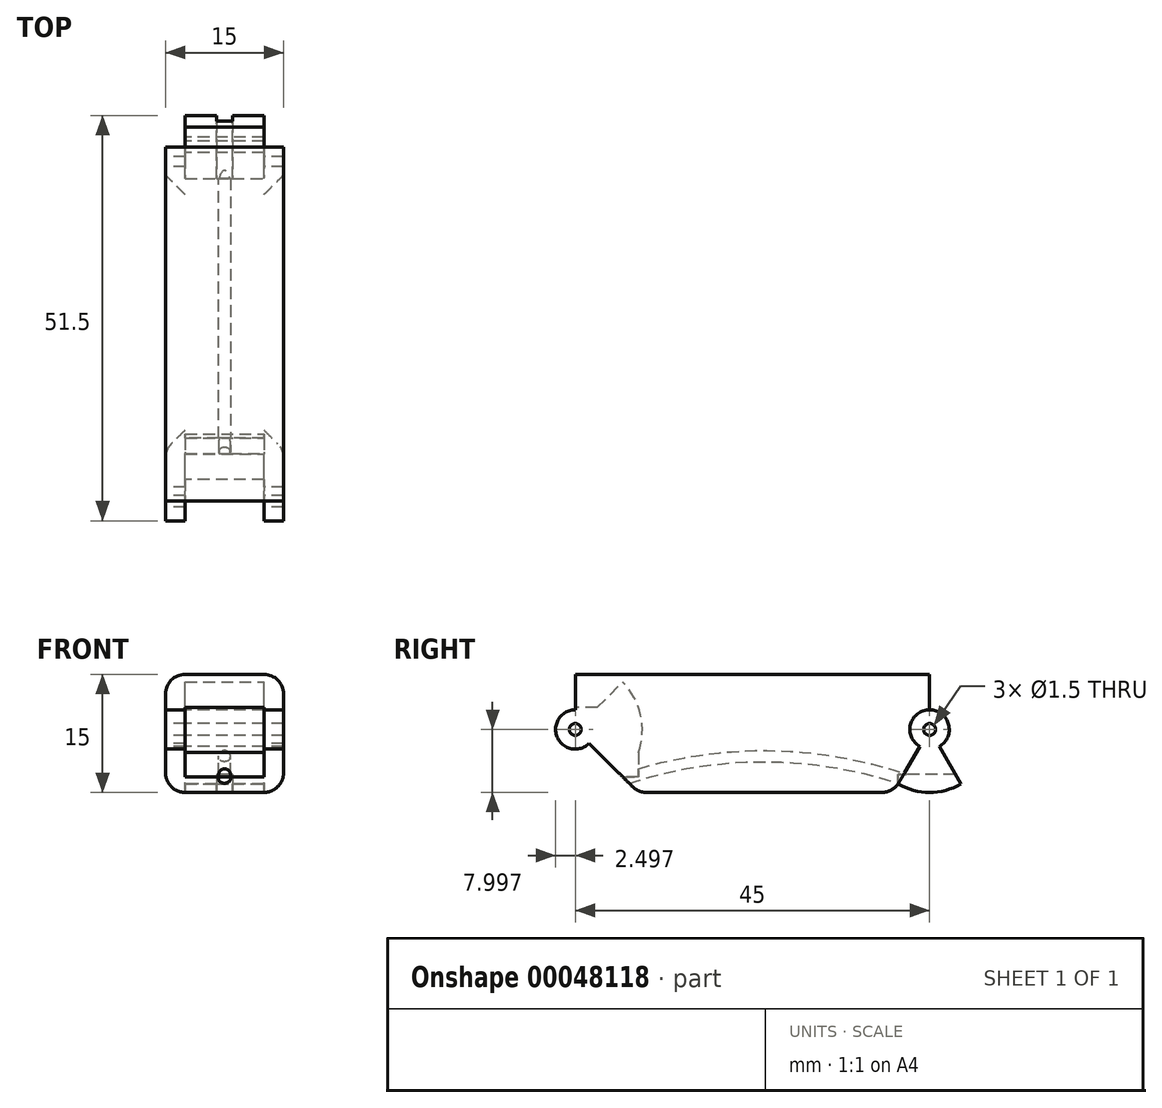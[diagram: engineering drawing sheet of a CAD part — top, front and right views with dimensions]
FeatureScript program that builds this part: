
annotation { "Feature Type Name" : "Feature", "Feature Type Description" : "" }
export const myFeature = defineFeature(function(context is Context, id is Id, definition is map)
    precondition{}
    {
        {
            var Q0;
            Q0=qCreatedBy(makeId("Right.planeOp"),FACE);
            var sketch = newSketch(context, id + "F0", { "sketchPlane" : qUnion([Q0])});
            skLineSegment(sketch, "E0.bottom", {"start": v(-42.54, 1.89) * mm, "end": v(2.46, 1.89) * mm});
            skLineSegment(sketch, "E0.top", {"start": v(-42.54, -13.11) * mm, "end": v(2.46, -13.11) * mm});
            skLineSegment(sketch, "E0.left", {"start": v(-42.54, 1.89) * mm, "end": v(-42.54, -13.11) * mm});
            skLineSegment(sketch, "E0.right", {"start": v(2.46, 1.89) * mm, "end": v(2.46, -13.11) * mm});
            skCircle(sketch, "E1", {"center": v(2.46, -5.11) * mm, "radius": 2.5 * mm});
            skCircle(sketch, "E2", {"center": v(2.46, -5.11) * mm, "radius": 8 * mm});
            skLineSegment(sketch, "E3", {"start": v(2.46, -5.11) * mm, "end": v(6.46, -12.04) * mm});
            skCircle(sketch, "E4", {"center": v(2.46, -5.11) * mm, "radius": 0.75 * mm});
            skLineSegment(sketch, "E5", {"start": v(2.46, -5.11) * mm, "end": v(-2.16, -13.11) * mm});
            skCircle(sketch, "E6", {"center": v(-42.54, -5.11) * mm, "radius": 2.5 * mm});
            skCircle(sketch, "E7", {"center": v(-42.54, -5.11) * mm, "radius": 0.75 * mm});
            skLineSegment(sketch, "E8", {"start": v(-42.54, -5.11) * mm, "end": v(-34.54, -13.11) * mm});
            skArc(sketch, "E9", {"start": v(-36.52, -11.13) * mm, "mid": v(-34.03, -5.11) * mm, "end": v(-36.52, 0.9) * mm});
            skLineSegment(sketch, "E10", {"start": v(-42.54, -5.11) * mm, "end": v(-35.54, 1.89) * mm});
            skSolve(sketch);
        }
        {
            var Q0;
            {var subQ3=sQuery(id+"F0.wireOp",EDGE,"E0.right");var subQ7=sQuery(id+"F0.wireOp",EDGE,"E0.bottom");var subQ8=makeQuery(id+"F0.imprint","INTERSECT",VERTEX,{"derivedFrom":[subQ7,subQ3]});Q0=makeQuery(id+"F0.imprint","IMPRINT",FACE,{"disambiguationData":[TD([[makeQuery(id+"F0.imprint","IMPRINT",EDGE,{"disambiguationData":[TD([[subQ8,1.0]])],"derivedFrom":subQ7}),-1.0]])]});}
            var Q1;
            {var subQ5=sQuery(id+"F0.wireOp",EDGE,"E0.left");var subQ11=sQuery(id+"F0.wireOp",EDGE,"E0.bottom");var subQ13=makeQuery(id+"F0.imprint","INTERSECT",VERTEX,{"derivedFrom":[subQ11,subQ5]});Q1=makeQuery(id+"F0.imprint","IMPRINT",FACE,{"disambiguationData":[TD([[makeQuery(id+"F0.imprint","IMPRINT",EDGE,{"disambiguationData":[TD([[subQ13,-1.0]])],"derivedFrom":subQ11}),-1.0]])]});}
            var Q2;
            {var subQ3=sQuery(id+"F0.wireOp",EDGE,"E6");var subQ5=sQuery(id+"F0.wireOp",EDGE,"E0.left");var subQ6=makeQuery(id+"F0.imprint","INTERSECT",VERTEX,{"disambiguationData":[OD(1.0)],"derivedFrom":[subQ5,subQ3]});Q2=makeQuery(id+"F0.imprint","IMPRINT",FACE,{"disambiguationData":[TD([[makeQuery(id+"F0.imprint","IMPRINT",EDGE,{"disambiguationData":[TD([[subQ6,1.0]])],"derivedFrom":subQ5}),1.0]])]});}
            var Q3;
            {var subQ1=sQuery(id+"F0.wireOp",EDGE,"E0.left");var subQ4=sQuery(id+"F0.wireOp",EDGE,"E6");var subQ6=makeQuery(id+"F0.imprint","INTERSECT",VERTEX,{"disambiguationData":[OD(0.0)],"derivedFrom":[subQ1,subQ4]});Q3=makeQuery(id+"F0.imprint","IMPRINT",FACE,{"disambiguationData":[TD([[makeQuery(id+"F0.imprint","IMPRINT",EDGE,{"disambiguationData":[TD([[subQ6,-1.0]])],"derivedFrom":subQ1}),-1.0]])]});}
            var Q4;
            {var subQ3=sQuery(id+"F0.wireOp",EDGE,"E6");var subQ5=sQuery(id+"F0.wireOp",EDGE,"E0.left");var subQ7=makeQuery(id+"F0.imprint","INTERSECT",VERTEX,{"disambiguationData":[OD(0.0)],"derivedFrom":[subQ5,subQ3]});Q4=makeQuery(id+"F0.imprint","IMPRINT",FACE,{"disambiguationData":[TD([[makeQuery(id+"F0.imprint","IMPRINT",EDGE,{"disambiguationData":[TD([[subQ7,-1.0]])],"derivedFrom":subQ5}),1.0]])]});}
            var Q5;
            {var subQ0=sQuery(id+"F0.wireOp",EDGE,"E9");Q5=makeQuery(id+"F0.imprint","IMPRINT",FACE,{"disambiguationData":[TD([[makeQuery(id+"F0.imprint","IMPRINT",EDGE,{"derivedFrom":subQ0}),-1.0]])]});}
            var Q6;
            {var subQ3=sQuery(id+"F0.wireOp",EDGE,"E9");Q6=makeQuery(id+"F0.imprint","IMPRINT",FACE,{"disambiguationData":[TD([[makeQuery(id+"F0.imprint","IMPRINT",EDGE,{"derivedFrom":subQ3}),1.0]])]});}
            var Q7;
            {var subQ0=sQuery(id+"F0.wireOp",EDGE,"E10");var subQ3=sQuery(id+"F0.wireOp",EDGE,"E6");var subQ4=makeQuery(id+"F0.imprint","INTERSECT",VERTEX,{"derivedFrom":[subQ3,subQ0]});Q7=makeQuery(id+"F0.imprint","IMPRINT",FACE,{"disambiguationData":[TD([[makeQuery(id+"F0.imprint","IMPRINT",EDGE,{"disambiguationData":[TD([[subQ4,1.0]])],"derivedFrom":subQ3}),1.0]])]});}
            extrude(context, id + "F1", {"entities" : qUnion([Q0, Q1, Q2, Q3, Q4, Q5, Q6, Q7]), "depth" : 15 * mm, "symmetric" : true});
        }
        {
            var Q0;
            {var subQ3=sQuery(id+"F0.wireOp",EDGE,"E1");var subQ5=sQuery(id+"F0.wireOp",EDGE,"E0.right");var subQ6=makeQuery(id+"F0.imprint","INTERSECT",VERTEX,{"disambiguationData":[OD(0.0)],"derivedFrom":[subQ5,subQ3]});Q0=makeQuery(id+"F0.imprint","IMPRINT",FACE,{"disambiguationData":[TD([[makeQuery(id+"F0.imprint","IMPRINT",EDGE,{"disambiguationData":[TD([[subQ6,-1.0]])],"derivedFrom":subQ5}),-1.0]])]});}
            var Q1;
            {var subQ3=sQuery(id+"F0.wireOp",EDGE,"E0.right");var subQ5=sQuery(id+"F0.wireOp",EDGE,"E1");var subQ7=makeQuery(id+"F0.imprint","INTERSECT",VERTEX,{"disambiguationData":[OD(0.0)],"derivedFrom":[subQ3,subQ5]});Q1=makeQuery(id+"F0.imprint","IMPRINT",FACE,{"disambiguationData":[TD([[makeQuery(id+"F0.imprint","IMPRINT",EDGE,{"disambiguationData":[TD([[subQ7,-1.0]])],"derivedFrom":subQ3}),1.0]])]});}
            var Q2;
            {var subQ1=sQuery(id+"F0.wireOp",EDGE,"E4");var subQ5=sQuery(id+"F0.wireOp",EDGE,"E0.right");var subQ7=makeQuery(id+"F0.imprint","INTERSECT",VERTEX,{"disambiguationData":[OD(1.0)],"derivedFrom":[subQ5,subQ1]});Q2=makeQuery(id+"F0.imprint","IMPRINT",FACE,{"disambiguationData":[TD([[makeQuery(id+"F0.imprint","IMPRINT",EDGE,{"disambiguationData":[TD([[subQ7,-1.0]])],"derivedFrom":subQ5}),1.0]])]});}
            var Q3;
            {var subQ0=sQuery(id+"F0.wireOp",EDGE,"E4");var subQ3=sQuery(id+"F0.wireOp",EDGE,"E0.right");var subQ4=makeQuery(id+"F0.imprint","INTERSECT",VERTEX,{"disambiguationData":[OD(1.0)],"derivedFrom":[subQ3,subQ0]});Q3=makeQuery(id+"F0.imprint","IMPRINT",FACE,{"disambiguationData":[TD([[makeQuery(id+"F0.imprint","IMPRINT",EDGE,{"disambiguationData":[TD([[subQ4,-1.0]])],"derivedFrom":subQ3}),-1.0]])]});}
            var Q4;
            {var subQ3=sQuery(id+"F0.wireOp",EDGE,"E0.right");var subQ5=sQuery(id+"F0.wireOp",EDGE,"E1");var subQ7=makeQuery(id+"F0.imprint","INTERSECT",VERTEX,{"disambiguationData":[OD(1.0)],"derivedFrom":[subQ3,subQ5]});Q4=makeQuery(id+"F0.imprint","IMPRINT",FACE,{"disambiguationData":[TD([[makeQuery(id+"F0.imprint","IMPRINT",EDGE,{"disambiguationData":[TD([[subQ7,1.0]])],"derivedFrom":subQ5}),-1.0]])]});}
            var Q5;
            {var subQ1=sQuery(id+"F0.wireOp",EDGE,"E1");var subQ5=sQuery(id+"F0.wireOp",EDGE,"E0.right");var subQ7=makeQuery(id+"F0.imprint","INTERSECT",VERTEX,{"disambiguationData":[OD(1.0)],"derivedFrom":[subQ5,subQ1]});Q5=makeQuery(id+"F0.imprint","IMPRINT",FACE,{"disambiguationData":[TD([[makeQuery(id+"F0.imprint","IMPRINT",EDGE,{"disambiguationData":[TD([[subQ7,-1.0]])],"derivedFrom":subQ1}),-1.0]])]});}
            extrude(context, id + "F2", {"entities" : qUnion([Q0, Q1, Q2, Q3, Q4, Q5]), "operationType" : NewBodyOperationType.ADD, "depth" : 10 * mm, "symmetric" : true});
        }
        {
            var Q0;
            Q0=qCreatedBy(makeId("Right.planeOp"),FACE);
            var sketch = newSketch(context, id + "F3", { "sketchPlane" : qUnion([Q0])});
            skCircle(sketch, "E11", {"center": v(-42.54, -5.11) * mm, "radius": 2.7 * mm});
            skSolve(sketch);
        }
        {
            var Q0;
            Q0=qSketchRegion(id+"F3",true);
            extrude(context, id + "F4", {"entities" : qUnion([Q0]), "operationType" : NewBodyOperationType.REMOVE, "oppositeDirection" : true, "depth" : 10 * mm, "symmetric" : true});
        }
        {
            var Q0;
            {var subQ0=sQuery(id+"F0.wireOp",EDGE,"E0.left");Q0=makeQuery(id+"F1.opExtrude","SWEPT_FACE",FACE,{"disambiguationData":[OSD([subQ0]),TDD([makeQuery(id+"F0.imprint","IMPRINT",EDGE,{"disambiguationData":[TD([[makeQuery(id+"F0.imprint","INTERSECT",VERTEX,{"derivedFrom":[sQuery(id+"F0.wireOp",EDGE,"E0.bottom"),subQ0]}),-1.0]])],"derivedFrom":subQ0})])]});}
            var sketch = newSketch(context, id + "F5", { "sketchPlane" : qUnion([Q0])});
            skLineSegment(sketch, "E12.bottom", {"start": v(5, -2.35) * mm, "end": v(-5, -2.35) * mm});
            skLineSegment(sketch, "E12.top", {"start": v(5, -11.11) * mm, "end": v(-5, -11.11) * mm});
            skLineSegment(sketch, "E12.left", {"start": v(5, -2.35) * mm, "end": v(5, -11.11) * mm});
            skLineSegment(sketch, "E12.right", {"start": v(-5, -2.35) * mm, "end": v(-5, -11.11) * mm});
            skSolve(sketch);
        }
        {
            var Q0;
            Q0=qSketchRegion(id+"F5",true);
            extrude(context, id + "F6", {"entities" : qUnion([Q0]), "operationType" : NewBodyOperationType.REMOVE, "oppositeDirection" : true, "depth" : 8 * mm});
        }
        {
            var Q0;
            {var subQ3=sQuery(id+"F0.wireOp",EDGE,"E9");Q0=makeQuery(id+"F0.imprint","IMPRINT",FACE,{"disambiguationData":[TD([[makeQuery(id+"F0.imprint","IMPRINT",EDGE,{"derivedFrom":subQ3}),1.0]])]});}
            extrude(context, id + "F7", {"entities" : qUnion([Q0]), "operationType" : NewBodyOperationType.REMOVE, "oppositeDirection" : true, "depth" : 10 * mm, "symmetric" : true});
        }
        {
            var Q0;
            Q0=makeQuery(id+"F1.opExtrude","SWEPT_FACE",FACE,{"disambiguationData":[OSD([sQuery(id+"F0.wireOp",EDGE,"E0.top")])]});
            var sketch = newSketch(context, id + "F8", { "sketchPlane" : qUnion([Q0])});
            skLineSegment(sketch, "E13.rect.bottom", {"start": v(-1, -6.46) * mm, "end": v(1, -6.46) * mm});
            skLineSegment(sketch, "E13.rect.top", {"start": v(-1, 1.54) * mm, "end": v(1, 1.54) * mm});
            skLineSegment(sketch, "E13.rect.left", {"start": v(-1, -6.46) * mm, "end": v(-1, 1.54) * mm});
            skLineSegment(sketch, "E13.rect.right", {"start": v(1, -6.46) * mm, "end": v(1, 1.54) * mm});
            skPoint(sketch, "E13.rect.middle", {"position": v(0, -2.46) * mm});
            skSolve(sketch);
        }
        {
            var Q0;
            Q0=qSketchRegion(id+"F8",true);
            extrude(context, id + "F9", {"entities" : qUnion([Q0]), "operationType" : NewBodyOperationType.REMOVE, "oppositeDirection" : true, "depth" : 2.3 * mm});
        }
        {
            var Q0;
            Q0=makeQuery(id+"F6.boolean.opBoolean","COPY",FACE,{"derivedFrom":makeQuery(id+"F6.opExtrude","CAP_FACE",FACE,{"disambiguationData":[OSD([sQuery(id+"F5.wireOp",EDGE,"E12.bottom"),sQuery(id+"F5.wireOp",EDGE,"E12.top"),sQuery(id+"F5.wireOp",EDGE,"E12.left"),sQuery(id+"F5.wireOp",EDGE,"E12.right")])],"isStart":false})});
            cPlane(context, id + "F10", {"entities" : qUnion([Q0]), "cplaneType" : CPlaneType.OFFSET, "offset" : 1.96 * mm, "width" : 150 * mm, "height" : 150 * mm});
        }
        {
            var Q0;
            Q0=qCreatedBy(id+"F10.planeOp",FACE);
            var sketch = newSketch(context, id + "F11", { "sketchPlane" : qUnion([Q0])});
            skCircle(sketch, "E14", {"center": v(0, -11.47) * mm, "radius": 0.75 * mm});
            skPoint(sketch, "E15", {"position": v(0, -11.11) * mm});
            skPoint(sketch, "E16", {"position": v(0, -13.1) * mm});
            skSolve(sketch);
        }
        {
            var Q0;
            Q0=qCreatedBy(makeId("Right.planeOp"),FACE);
            var sketch = newSketch(context, id + "F12", { "sketchPlane" : qUnion([Q0])});
            skArc(sketch, "E17", {"start": v(-0.79, -11.47) * mm, "mid": v(-18.64, -8.5) * mm, "end": v(-36.5, -11.47) * mm});
            skSolve(sketch);
        }
        {
            var Q0;
            Q0=qSketchRegion(id+"F11",true);
            var Q1;
            Q1=qConstructionFilter(qBodyType(qCreatedBy(id+"F12",EDGE),BodyType.WIRE),ConstructionObject.NO);
            sweep(context, id + "F13", {"operationType" : NewBodyOperationType.REMOVE, "profiles" : qUnion([Q0]), "path" : qUnion([Q1])});
        }
        {
            var Q0;
            Q0=makeQuery(id+"F1.opExtrude","CAP_EDGE",EDGE,{"disambiguationData":[OSD([sQuery(id+"F0.wireOp",EDGE,"E0.bottom")])],"isStart":false});
            var Q1;
            Q1=makeQuery(id+"F1.opExtrude","CAP_EDGE",EDGE,{"disambiguationData":[OSD([sQuery(id+"F0.wireOp",EDGE,"E0.top")])],"isStart":false});
            var Q2;
            Q2=makeQuery(id+"F1.opExtrude","CAP_EDGE",EDGE,{"disambiguationData":[OSD([sQuery(id+"F0.wireOp",EDGE,"E0.bottom")])],"isStart":true});
            var Q3;
            Q3=makeQuery(id+"F1.opExtrude","CAP_EDGE",EDGE,{"disambiguationData":[OSD([sQuery(id+"F0.wireOp",EDGE,"E0.top")])],"isStart":true});
            var Q4;
            Q4=makeQuery(id+"F1.opExtrude","SWEPT_EDGE",EDGE,{"disambiguationData":[OSD([sQuery(id+"F0.wireOp",EDGE,"E0.top"),sQuery(id+"F0.wireOp",EDGE,"E8")])]});
            var Q5;
            Q5=makeQuery(id+"F1.opExtrude","SWEPT_EDGE",EDGE,{"disambiguationData":[OSD([sQuery(id+"F0.wireOp",EDGE,"E0.top"),sQuery(id+"F0.wireOp",EDGE,"E5")])]});
            fillet(context, id + "F14", {"entities" : qUnion([Q0, Q1, Q2, Q3, Q4, Q5]), "radius" : 2.5 * mm, "tangentPropagation" : true, "allowEdgeOverflow" : false});
        }
    });
